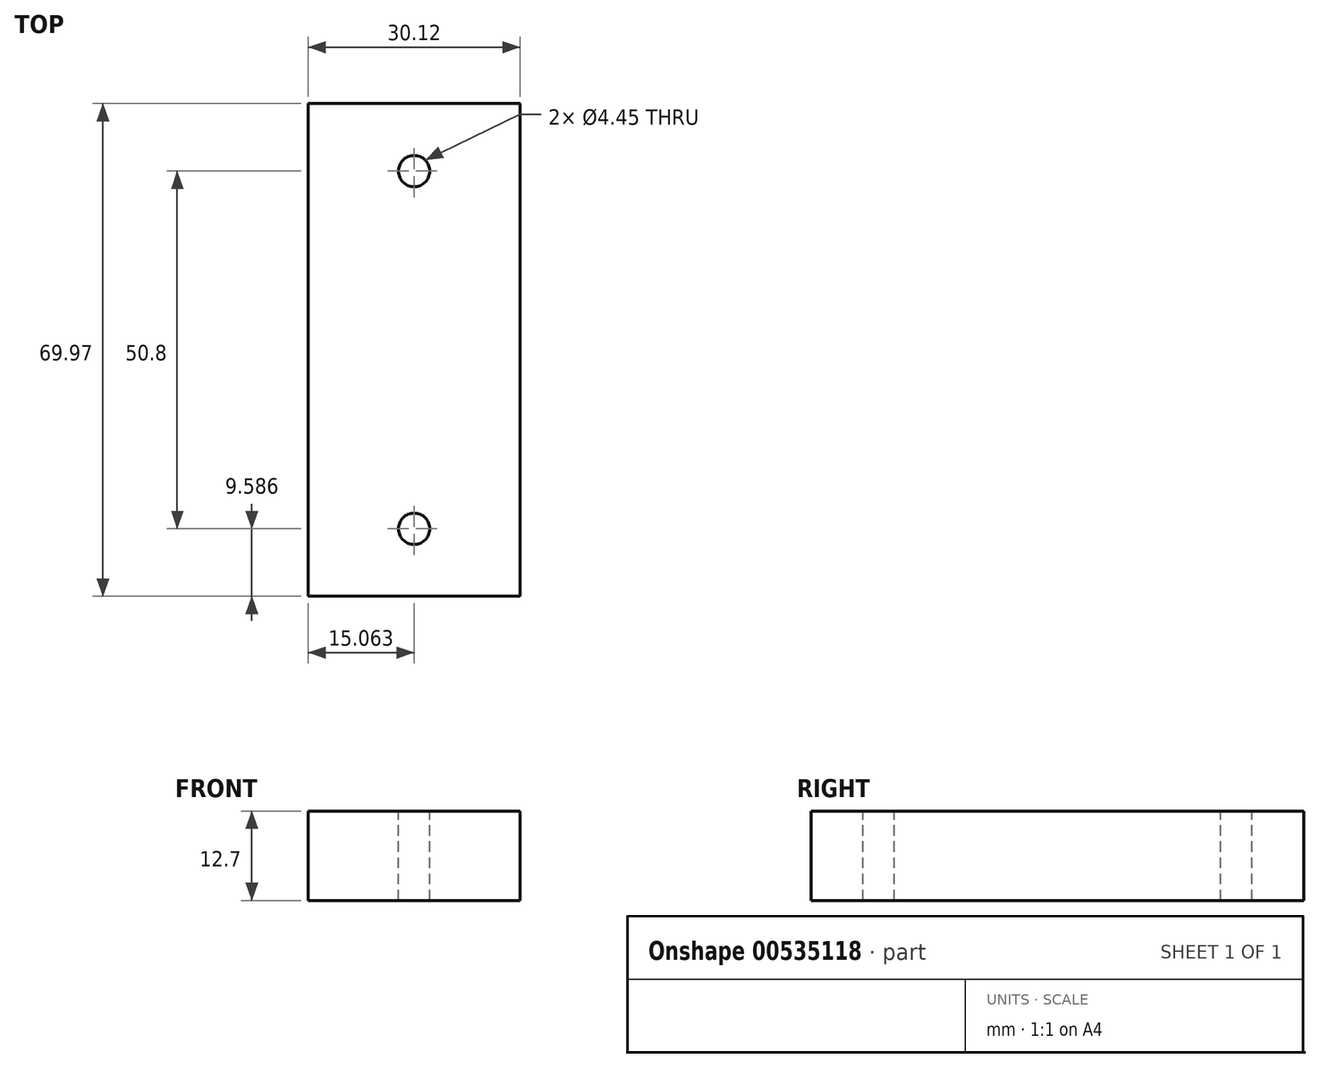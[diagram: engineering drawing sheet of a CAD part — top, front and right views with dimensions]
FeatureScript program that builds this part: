
annotation { "Feature Type Name" : "Feature", "Feature Type Description" : "" }
export const myFeature = defineFeature(function(context is Context, id is Id, definition is map)
    precondition{}
    {
        {
            var Q0;
            Q0=qCreatedBy(makeId("Top.planeOp"),FACE);
            var sketch = newSketch(context, id + "F0", { "sketchPlane" : qUnion([Q0])});
            skLineSegment(sketch, "E0.bottom", {"start": v(-40.24, 41.83) * mm, "end": v(-70.36, 41.83) * mm});
            skLineSegment(sketch, "E0.top", {"start": v(-40.24, -28.14) * mm, "end": v(-70.36, -28.14) * mm});
            skLineSegment(sketch, "E0.left", {"start": v(-40.24, 41.83) * mm, "end": v(-40.24, -28.14) * mm});
            skLineSegment(sketch, "E0.right", {"start": v(-70.36, 41.83) * mm, "end": v(-70.36, -28.14) * mm});
            skSolve(sketch);
        }
        {
            var Q0;
            Q0=qSketchRegion(id+"F0",true);
            extrude(context, id + "F1", {"entities" : qUnion([Q0]), "depth" : 12.7 * mm});
        }
        {
            var Q0;
            Q0=makeQuery(id+"F1.opExtrude","CAP_FACE",FACE,{"disambiguationData":[OSD([sQuery(id+"F0.wireOp",EDGE,"E0.bottom"),sQuery(id+"F0.wireOp",EDGE,"E0.top"),sQuery(id+"F0.wireOp",EDGE,"E0.left"),sQuery(id+"F0.wireOp",EDGE,"E0.right")])],"isStart":false});
            var sketch = newSketch(context, id + "F2", { "sketchPlane" : qUnion([Q0])});
            skCircle(sketch, "E1", {"center": v(-55.3, -18.55) * mm, "radius": 2.22 * mm});
            skCircle(sketch, "E2", {"center": v(-55.3, 32.25) * mm, "radius": 2.22 * mm});
            skLineSegment(sketch, "E3", {"start": v(-55.3, 7.18) * mm, "end": v(-55.3, -44.29) * mm, "construction": true});
            skLineSegment(sketch, "E4", {"start": v(-89.14, 6.85) * mm, "end": v(-40.05, 6.85) * mm, "construction": true});
            skPoint(sketch, "E5", {"position": v(-55.3, -28.14) * mm});
            skSolve(sketch);
        }
        {
            var Q0;
            Q0=qSketchRegion(id+"F2",true);
            extrude(context, id + "F3", {"entities" : qUnion([Q0]), "operationType" : NewBodyOperationType.REMOVE, "oppositeDirection" : true, "depth" : 25.4 * mm});
        }
    });
